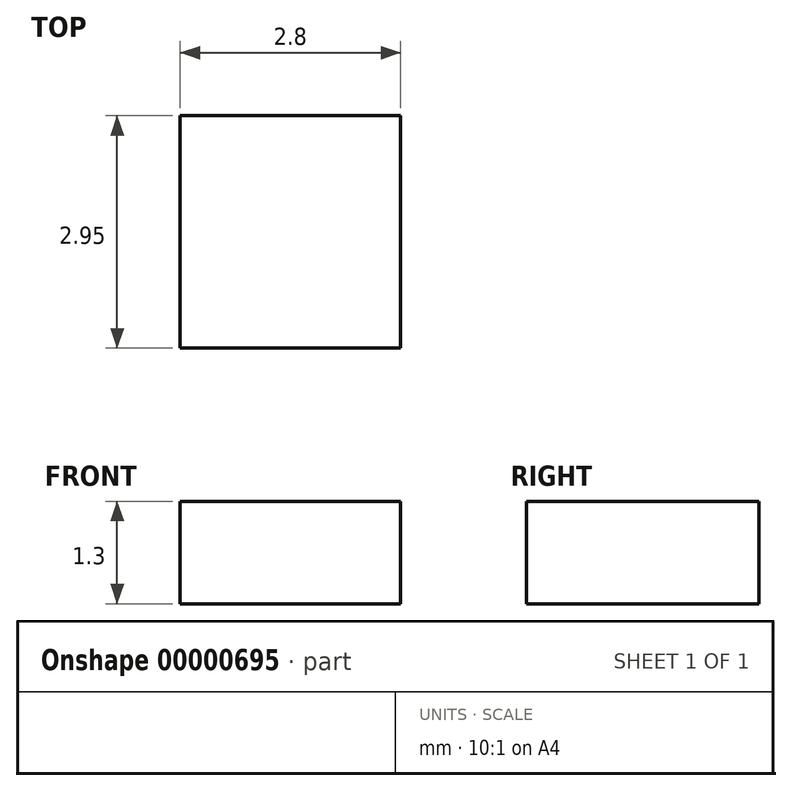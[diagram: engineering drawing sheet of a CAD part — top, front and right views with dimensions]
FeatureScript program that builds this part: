
annotation { "Feature Type Name" : "Feature", "Feature Type Description" : "" }
export const myFeature = defineFeature(function(context is Context, id is Id, definition is map)
    precondition{}
    {
        {
            var Q0;
            Q0=qCreatedBy(makeId("Top.planeOp"),FACE);
            var sketch = newSketch(context, id + "F0", { "sketchPlane" : qUnion([Q0])});
            skLineSegment(sketch, "E0.bottom", {"start": v(0, 0) * mm, "end": v(2.8, 0) * mm});
            skLineSegment(sketch, "E0.top", {"start": v(0, 2.95) * mm, "end": v(2.8, 2.95) * mm});
            skLineSegment(sketch, "E0.left", {"start": v(0, 0) * mm, "end": v(0, 2.95) * mm});
            skLineSegment(sketch, "E0.right", {"start": v(2.8, 0) * mm, "end": v(2.8, 2.95) * mm});
            skSolve(sketch);
        }
        {
            var Q0;
            Q0=makeQuery(id+"F0.imprint","IMPRINT",FACE,{"disambiguationData":[TD([[makeQuery(id+"F0.imprint","IMPRINT",EDGE,{"derivedFrom":sQuery(id+"F0.wireOp",EDGE,"E0.bottom")}),1.0]])]});
            extrude(context, id + "F1", {"entities" : qUnion([Q0]), "depth" : 1.3 * mm});
        }
    });
